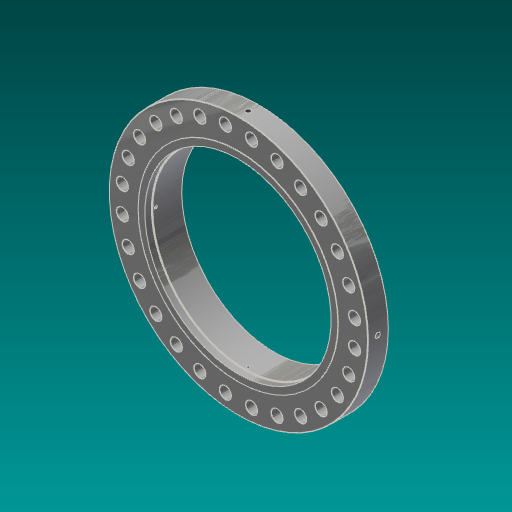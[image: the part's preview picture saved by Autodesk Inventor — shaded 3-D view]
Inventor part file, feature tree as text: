
AUTODESK INVENTOR PART (.ipt)
format: ipt  version: 2017.3 (Build 213256000, 256)  size: 418,816 bytes
history: native  units: in
note: dims shown in document units (in); Inventor stores cm internally (conversion verified against a paired STEP export)
features: sketch x6, hole x4, chamfer x4, extrude x3, pattern_circular x2, fillet x2, revolve x1, plane x1, projected_geometry x1
ambient origin geometry x8: Origin, YZ Plane, XZ Plane, XY Plane, X Axis, Y Axis, Z Axis, Center Point
bodies: Solid1 (feature_tree)
feature tree (24):
  extrude  "Extrusion1"  Depth=27.25in
  extrude  "Extrusion2"  Depth=29.5in
  extrude  "Extrusion3"  Depth=30.25in
  hole  "Hole1"  [1 undecoded]
  chamfer  "Chamfer3"  Distance=11.0236in Angle=360.0deg
  pattern_circular  "Circular Pattern1"  [2 undecoded]
  chamfer  "Chamfer2"  Distance=0.0312in Angle=45.0deg
  fillet  "Fillet2"  Radius=0.0625in
  chamfer  "Chamfer4"  Distance=0.2577in
  revolve  "Revolution1"  Angle=90.0deg
  fillet  "Fillet5"  Radius=0.25in
  chamfer  "Chamfer7"  Distance=0.6875in
  plane  "Work Plane1"
  sketch  "Sketch11"  dims[d25=0.0625in d26=0.125in d27=0.0687in d29=0.375in d30=0.0312in d31=0.125in d32=45.0deg d33=0.0625in d34=0.125in d35=45.0deg d45=0.2577in d49=90.0deg d59=0.25in d69=0.6875in d70=0.125in d71=1.0in d72=13.75in d73=0.0312in d74=0.0312in d75=0.125in d76=45.0deg d96=15.0in d97=0.5in d98=1.0in d99=0.0442in d101=0.5in d102=0.688in d103=0.534in d104=0.0246in d105=0.688in d106=0.375in d107=0.25in d108=0.5635in d109=0.891in d110=0.8108in d111=0.417in d112=1.0in d113=0.375in d114=0.25in d115=0.5635in d116=1.5in d117=0.8108in d118=0.4062in d119=1.0in d120=0.375in d121=0.25in d122=0.5635in d123=6.0in d124=0.8108in d125=1.5748in d126=360.0deg]
  hole  "Hole4"  [1 undecoded]
  hole  "Hole5"  [1 undecoded]
  hole  "Hole6"  [1 undecoded]
  pattern_circular  "Circular Pattern3"  [2 undecoded]
  sketch  "Sketch1"  dims[d0=38.25in d1=27.25in]
  sketch  "Sketch2"  dims[d2=3.0625in d3=0.0in d4=29.5in]
  sketch  "Sketch3"  dims[d5=0.0625in d6=0.0in d7=30.25in]
  sketch  "Sketch4"  dims[d8=2.1875in d9=0.0in d13=17.25in]
  sketch  "Sketch6"  dims[d15=1.75in d16=0.75in d17=0.375in d18=0.25in d19=0.5635in d20=1.0in d21=0.8108in d22=11.0236in d23=360.0deg]
  projected_geometry  "Projected Loop1"
note: 8 required parameter values undecoded (feature->parameter linkage not recoverable at this tier; creation-order binding heuristic only, values carry confidence <= 0.55)
